# Revit family: BIMLIB_ГибкаяВставка_FKr_SHUFT
name_source: partatom
category: Арматура воздуховодов
revit_build: Autodesk Revit 2017 (Build: 20170118_1100(x64)
units: mm (PartAtom-declared; Revit-internal decimal feet)

## family parameters
Всегда вертикально = Да
На основе рабочей плоскости = Нет
Общий = Нет
При загрузке вырезать с полостями = Нет
Размер круглого соединителя = Использовать диаметр
Тип детали = Вставляется

## types (1)
- BIMLIB_ГибкаяВставка_FKr_SHUFT
    ADSK_URL документации изделия = http://www.shuft.ru
    ADSK_URL страницы изделия = http://www.shuft.ru
    ADSK_Версия Revit = 2017
    ADSK_Версия семейства = v.1
    ADSK_Единица измерения = шт.
    ADSK_Завод-изготовитель = ООО «Завод ВКО» марка SHUFT
    ADSK_Материал = BIMLIB_Сталь_SHUFT
    ADSK_Размер_Длина = 130 мм
    BL_BIM library = https://bimlib.pro
    URL = http://www.shuft.ru
    Изготовитель = ООО «Завод ВКО» марка SHUFT
    Описание = Гибкие вставки серии FKr для прямоугольных воздуховодов предназначены для соединения различных элементов вентиляционных систем прямоугольного сечения соответствующего типоразмера.

Выполняют функцию вибропоглощения для пресечения распространения вибрации отдельных элементов на всю вентиляционную систему.

Корпус вставки выполнен из оцинкованной стали, в середине закреплена лента ПВХ, обеспечивающая герметичность канала.
    Таблица = FKr
